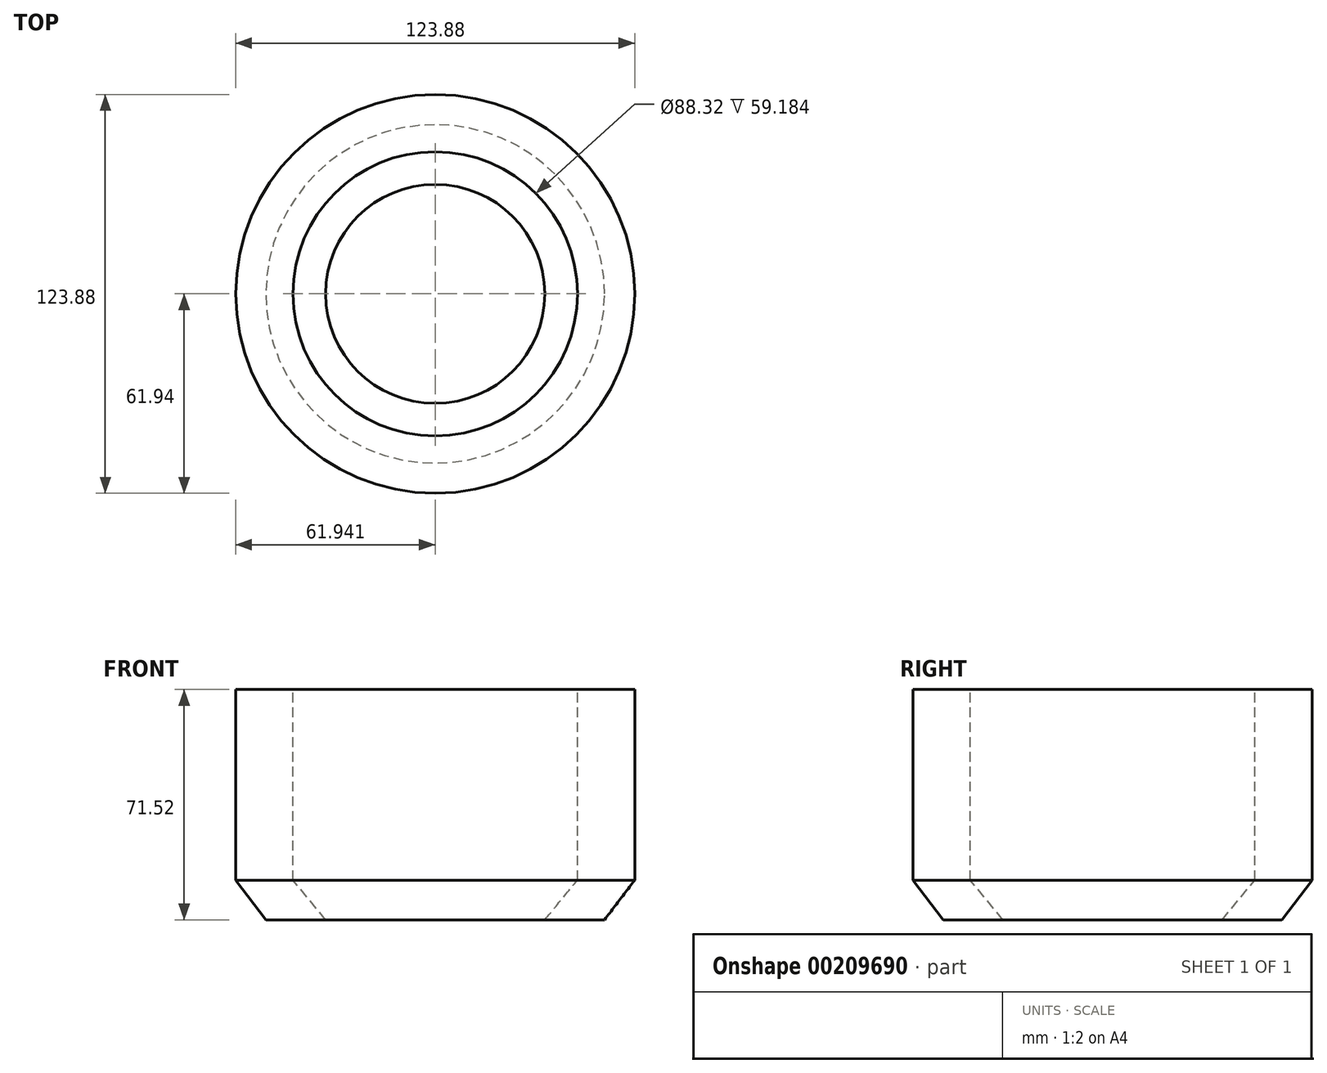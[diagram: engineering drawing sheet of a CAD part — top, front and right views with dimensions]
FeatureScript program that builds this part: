
annotation { "Feature Type Name" : "Feature", "Feature Type Description" : "" }
export const myFeature = defineFeature(function(context is Context, id is Id, definition is map)
    precondition{}
    {
        {
            var Q0;
            Q0=qCreatedBy(makeId("Front.planeOp"),FACE);
            var sketch = newSketch(context, id + "F0", { "sketchPlane" : qUnion([Q0])});
            skLineSegment(sketch, "E0", {"start": v(35.56, 71.52) * mm, "end": v(35.56, 12.33) * mm});
            skLineSegment(sketch, "E1", {"start": v(35.56, 12.33) * mm, "end": v(26.2, 0) * mm});
            skLineSegment(sketch, "E2", {"start": v(35.56, 71.52) * mm, "end": v(17.78, 71.52) * mm});
            skLineSegment(sketch, "E3", {"start": v(17.78, 71.52) * mm, "end": v(17.78, 12.33) * mm});
            skLineSegment(sketch, "E4", {"start": v(17.78, 12.33) * mm, "end": v(7.65, 0) * mm});
            skLineSegment(sketch, "E5", {"start": v(7.65, 0) * mm, "end": v(26.2, 0) * mm});
            skLineSegment(sketch, "E6", {"start": v(-26.38, 71.52) * mm, "end": v(-26.38, 0) * mm, "construction": true});
            skPoint(sketch, "E7", {"position": v(26.67, 71.52) * mm});
            skLineSegment(sketch, "E8", {"start": v(-26.38, 49.9) * mm, "end": v(35.56, 49.9) * mm, "construction": true});
            skLineSegment(sketch, "E9", {"start": v(17.78, 31.8) * mm, "end": v(-26.38, 31.8) * mm, "construction": true});
            skSolve(sketch);
        }
        {
            var Q0;
            Q0=makeQuery(id+"F0.imprint","IMPRINT",FACE,{"disambiguationData":[TD([[makeQuery(id+"F0.imprint","IMPRINT",EDGE,{"derivedFrom":sQuery(id+"F0.wireOp",EDGE,"E0")}),-1.0]])]});
            var Q1;
            Q1=sQuery(id+"F0.wireOp",EDGE,"E6");
            revolve(context, id + "F1", {"entities" : qUnion([Q0]), "axis" : qUnion([Q1]), "revolveType" : RevolveType.FULL});
        }
    });
